FCSTD DOCUMENT  (FreeCAD 1.0R39109 (Git))
Label: servo_reduced
License: All rights reserved
LicenseURL: https://en.wikipedia.org/wiki/All_rights_reserved
objects: Sketcher::SketchObject×1, PartDesign::Body×1
note: 3 computed .brp shape members not serialized (recipe doc carries the construction recipe); baked Part::Feature solids carry a one-line shape summary decoded from their .brp

FEATURE [Sketcher::SketchObject] Sketch
  ArcFitTolerance = 1e-06
  AttachmentSupport = -> [XY_Plane]
  FullyConstrained = false
  MakeInternals = false
  MapMode = 5
  sketch-geometry (18):
    g0: LineSegment StartX=0 StartY=0 StartZ=0 EndX=40.2 EndY=0 EndZ=0
    g1: LineSegment StartX=40.2 StartY=0 StartZ=0 EndX=40.2 EndY=61.1 EndZ=0
    g2: LineSegment StartX=40.2 StartY=61.1 StartZ=0 EndX=25.2962 EndY=61.1 EndZ=0
    g3: LineSegment StartX=0 StartY=61.1 StartZ=0 EndX=0 EndY=0 EndZ=0
    g4: ArcOfCircle CenterX=20.1 CenterY=48.1 CenterZ=0 NormalX=0 NormalY=0 NormalZ=1 AngleXU=0 Radius=14 StartAngle=1.19055 EndAngle=1.95105
    g5: LineSegment [constr] StartX=20.1 StartY=5.6 StartZ=0 EndX=34.6 EndY=5.6 EndZ=0
    g6: LineSegment StartX=34.6 StartY=5.6 StartZ=0 EndX=5.6 EndY=5.6 EndZ=0
    g7: LineSegment StartX=5.6 StartY=5.6 StartZ=0 EndX=5.6 EndY=61.1 EndZ=0
    g8: LineSegment StartX=34.6 StartY=5.6 StartZ=0 EndX=34.6 EndY=61.1 EndZ=0
    g9: Circle CenterX=31.1 CenterY=2.8 CenterZ=0 NormalX=0 NormalY=0 NormalZ=1 AngleXU=0 Radius=1.25
    g10: Circle CenterX=9.1 CenterY=2.8 CenterZ=0 NormalX=0 NormalY=0 NormalZ=1 AngleXU=0 Radius=1.25
    g11: Circle CenterX=2.8 CenterY=52.1 CenterZ=0 NormalX=0 NormalY=0 NormalZ=1 AngleXU=0 Radius=1.25
    g12: Circle CenterX=37.4 CenterY=52.1 CenterZ=0 NormalX=0 NormalY=0 NormalZ=1 AngleXU=0 Radius=1.25
    g13: Circle CenterX=2.8 CenterY=30.1 CenterZ=0 NormalX=0 NormalY=0 NormalZ=1 AngleXU=0 Radius=1.25
    g14: Circle CenterX=2.8 CenterY=8.1 CenterZ=0 NormalX=0 NormalY=0 NormalZ=1 AngleXU=0 Radius=1.25
    g15: Circle CenterX=37.4 CenterY=30.1 CenterZ=0 NormalX=0 NormalY=0 NormalZ=1 AngleXU=0 Radius=1.25
    g16: Circle CenterX=37.4 CenterY=8.1 CenterZ=0 NormalX=0 NormalY=0 NormalZ=1 AngleXU=0 Radius=1.25
    g17: LineSegment StartX=14.9038 StartY=61.1 StartZ=0 EndX=0 EndY=61.1 EndZ=0
  constraints (31):
    c: Coincident(g0,g1)
    c: Coincident(g1,g2)
    c: Coincident(g17,g3)
    c: Coincident(g3,g0)
    c: Horizontal(g0)
    c: Horizontal(g2)
    c: Vertical(g1)
    c: Vertical(g3)
    c: Distance(g1,g3) = 40.2
    c: Distance(g0,g17) = 61.1
    c: Coincident(g0,g-1)
    c: Diameter(g4) = 28
    c: Horizontal(g5)
    c: Coincident(g6,g5)
    c: Horizontal(g6)
    c: Coincident(g7,g6)
    c: PointOnObject(g7,g17)
    c: Vertical(g7)
    c: Coincident(g8,g5)
    c: PointOnObject(g8,g2)
    c: Vertical(g8)
    c: Diameter(g9) = 2.5
    c: Equal(g9,g10)
    c: Equal(g9,g12)
    c: Equal(g9,g11)
    c: Equal(g9,g13)
    c: Equal(g9,g14)
    c: Equal(g9,g16)
    c: Equal(g9,g15)
    c: Coincident(g4,g17)
    c: Coincident(g4,g2)
FEATURE [PartDesign::Body] Body
  AllowCompound = false
  Group = -> [Sketch]
  Origin = -> Origin
